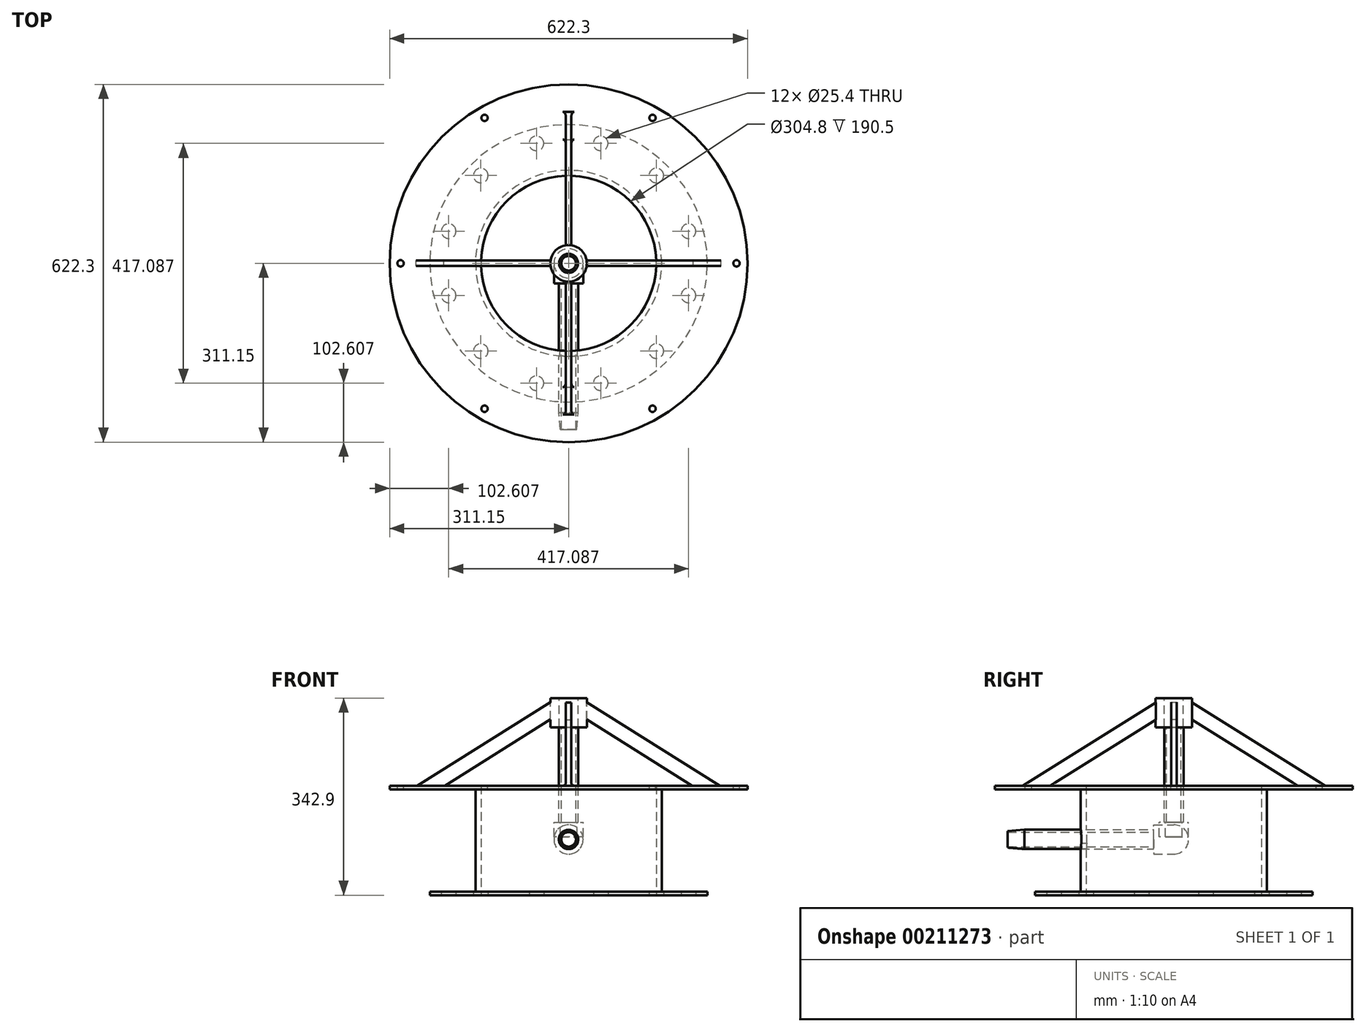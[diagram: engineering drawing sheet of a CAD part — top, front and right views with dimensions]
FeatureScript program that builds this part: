
annotation { "Feature Type Name" : "Feature", "Feature Type Description" : "" }
export const myFeature = defineFeature(function(context is Context, id is Id, definition is map)
    precondition{}
    {
        {
            var Q0;
            Q0=qCreatedBy(makeId("Top.planeOp"),FACE);
            var sketch = newSketch(context, id + "F0", { "sketchPlane" : qUnion([Q0])});
            skCircle(sketch, "E0", {"center": v(0, 0) * mm, "radius": 241.3 * mm});
            skCircle(sketch, "E1", {"center": v(0, 0) * mm, "radius": 152.4 * mm});
            skCircle(sketch, "E2", {"center": v(55.88, 208.54) * mm, "radius": 12.7 * mm});
            skCircle(sketch, "E3.1.0", {"center": v(-55.88, 208.54) * mm, "radius": 12.7 * mm});
            skCircle(sketch, "E3.2.0", {"center": v(-152.66, 152.66) * mm, "radius": 12.7 * mm});
            skCircle(sketch, "E3.3.0", {"center": v(-208.54, 55.88) * mm, "radius": 12.7 * mm});
            skCircle(sketch, "E3.4.0", {"center": v(-208.54, -55.88) * mm, "radius": 12.7 * mm});
            skCircle(sketch, "E3.5.0", {"center": v(-152.66, -152.66) * mm, "radius": 12.7 * mm});
            skCircle(sketch, "E3.6.0", {"center": v(-55.88, -208.54) * mm, "radius": 12.7 * mm});
            skCircle(sketch, "E3.7.0", {"center": v(55.88, -208.54) * mm, "radius": 12.7 * mm});
            skCircle(sketch, "E3.8.0", {"center": v(152.66, -152.66) * mm, "radius": 12.7 * mm});
            skCircle(sketch, "E3.9.0", {"center": v(208.54, -55.88) * mm, "radius": 12.7 * mm});
            skCircle(sketch, "E3.10.0", {"center": v(208.54, 55.88) * mm, "radius": 12.7 * mm});
            skCircle(sketch, "E3.11.0", {"center": v(152.66, 152.66) * mm, "radius": 12.7 * mm});
            skSolve(sketch);
        }
        {
            var Q0;
            Q0 = qSketchRegion(id + "F0", true);
            extrude(context, id + "F1", {"entities" : qUnion([Q0]), "depth" : 6.35 * mm});
        }
        {
            var Q0;
            Q0=makeQuery(id+"F1.opExtrude","CAP_FACE",FACE,{"disambiguationData":[OSD([sQuery(id+"F0.wireOp",EDGE,"E0"),sQuery(id+"F0.wireOp",EDGE,"E1"),sQuery(id+"F0.wireOp",EDGE,"E2"),sQuery(id+"F0.wireOp",EDGE,"E3.1.0"),sQuery(id+"F0.wireOp",EDGE,"E3.2.0"),sQuery(id+"F0.wireOp",EDGE,"E3.3.0"),sQuery(id+"F0.wireOp",EDGE,"E3.4.0"),sQuery(id+"F0.wireOp",EDGE,"E3.5.0"),sQuery(id+"F0.wireOp",EDGE,"E3.6.0"),sQuery(id+"F0.wireOp",EDGE,"E3.7.0"),sQuery(id+"F0.wireOp",EDGE,"E3.8.0"),sQuery(id+"F0.wireOp",EDGE,"E3.9.0"),sQuery(id+"F0.wireOp",EDGE,"E3.10.0"),sQuery(id+"F0.wireOp",EDGE,"E3.11.0")])],"isStart":false});
            var sketch = newSketch(context, id + "F2", { "sketchPlane" : qUnion([Q0])});
            skCircle(sketch, "E4", {"center": v(0, 0) * mm, "radius": 152.4 * mm});
            skCircle(sketch, "E5", {"center": v(0, 0) * mm, "radius": 161.93 * mm});
            skSolve(sketch);
        }
        {
            var Q0;
            Q0 = qSketchRegion(id + "F2", true);
            extrude(context, id + "F3", {"entities" : qUnion([Q0]), "operationType" : NewBodyOperationType.ADD, "depth" : 177.8 * mm});
        }
        {
            var Q0;
            Q0=makeQuery(id+"F3.opExtrude","CAP_FACE",FACE,{"disambiguationData":[OSD([sQuery(id+"F2.wireOp",EDGE,"E4"),sQuery(id+"F2.wireOp",EDGE,"E5")])],"isStart":false});
            var sketch = newSketch(context, id + "F4", { "sketchPlane" : qUnion([Q0])});
            skCircle(sketch, "E6", {"center": v(0, 0) * mm, "radius": 311.15 * mm});
            skCircle(sketch, "E7", {"center": v(0, 0) * mm, "radius": 152.4 * mm});
            skSolve(sketch);
        }
        {
            var Q0;
            Q0 = qSketchRegion(id + "F4", true);
            extrude(context, id + "F5", {"entities" : qUnion([Q0]), "operationType" : NewBodyOperationType.ADD, "depth" : 6.35 * mm});
        }
        {
            var Q0;
            Q0=makeQuery(id+"F5.opExtrude","CAP_FACE",FACE,{"disambiguationData":[OSD([sQuery(id+"F4.wireOp",EDGE,"E6"),sQuery(id+"F4.wireOp",EDGE,"E7")])],"isStart":false});
            var sketch = newSketch(context, id + "F6", { "sketchPlane" : qUnion([Q0])});
            skCircle(sketch, "E8", {"center": v(146.05, 252.97) * mm, "radius": 5.56 * mm});
            skCircle(sketch, "E9.1.0", {"center": v(-146.05, 252.97) * mm, "radius": 5.56 * mm});
            skCircle(sketch, "E9.2.0", {"center": v(-292.1, 0) * mm, "radius": 5.56 * mm});
            skCircle(sketch, "E9.3.0", {"center": v(-146.05, -252.97) * mm, "radius": 5.56 * mm});
            skCircle(sketch, "E9.4.0", {"center": v(146.05, -252.97) * mm, "radius": 5.56 * mm});
            skCircle(sketch, "E9.5.0", {"center": v(292.1, 0) * mm, "radius": 5.56 * mm});
            skPoint(sketch, "E9.center", {"position": v(0, 0) * mm});
            skSolve(sketch);
        }
        {
            var Q0;
            Q0 = qSketchRegion(id + "F6", true);
            extrude(context, id + "F7", {"entities" : qUnion([Q0]), "operationType" : NewBodyOperationType.REMOVE, "oppositeDirection" : true, "depth" : 25.4 * mm});
        }
        {
            var Q0;
            Q0=makeQuery(id+"F5.opExtrude","CAP_FACE",FACE,{"disambiguationData":[OSD([sQuery(id+"F4.wireOp",EDGE,"E6"),sQuery(id+"F4.wireOp",EDGE,"E7")])],"isStart":false});
            cPlane(context, id + "F8", {"entities" : qUnion([Q0]), "cplaneType" : CPlaneType.OFFSET, "offset" : 152.4 * mm, "width" : 152.4 * mm, "height" : 152.4 * mm});
        }
        {
            var Q0;
            Q0=qCreatedBy(id+"F8.planeOp",FACE);
            var sketch = newSketch(context, id + "F9", { "sketchPlane" : qUnion([Q0])});
            skCircle(sketch, "E10", {"center": v(0, 0) * mm, "radius": 16.51 * mm});
            skCircle(sketch, "E11", {"center": v(0, 0) * mm, "radius": 31.75 * mm});
            skSolve(sketch);
        }
        {
            var Q0;
            Q0 = qSketchRegion(id + "F9", true);
            extrude(context, id + "F10", {"entities" : qUnion([Q0]), "oppositeDirection" : true, "depth" : 50.8 * mm});
        }
        {
            var Q0;
            Q0=qCreatedBy(makeId("Front.planeOp"),FACE);
            var sketch = newSketch(context, id + "F11", { "sketchPlane" : qUnion([Q0])});
            skLineSegment(sketch, "E12", {"start": v(-31.31, 335.52) * mm, "end": v(-264.9, 189.3) * mm});
            skLineSegment(sketch, "E13", {"start": v(-264.9, 189.3) * mm, "end": v(-217.03, 189.3) * mm});
            skLineSegment(sketch, "E14", {"start": v(-217.03, 189.3) * mm, "end": v(-31.31, 305.55) * mm});
            skLineSegment(sketch, "E15", {"start": v(-31.31, 305.55) * mm, "end": v(-31.31, 335.52) * mm});
            skLineSegment(sketch, "E16", {"start": v(0, 0) * mm, "end": v(0, 440.85) * mm});
            skLineSegment(sketch, "E17.MirrorCS", {"start": v(217.03, 189.3) * mm, "end": v(31.31, 305.55) * mm});
            skLineSegment(sketch, "E18.MirrorCS", {"start": v(31.31, 335.52) * mm, "end": v(264.9, 189.3) * mm});
            skLineSegment(sketch, "E19.MirrorCS", {"start": v(31.31, 305.55) * mm, "end": v(31.31, 335.52) * mm});
            skLineSegment(sketch, "E20.MirrorCS", {"start": v(264.9, 189.3) * mm, "end": v(217.03, 189.3) * mm});
            skSolve(sketch);
        }
        {
            var Q0;
            Q0=makeQuery(id+"F11.imprint","IMPRINT",FACE,{"disambiguationData":[TD([[makeQuery(id+"F11.imprint","IMPRINT",EDGE,{"derivedFrom":sQuery(id+"F11.wireOp",EDGE,"E12")}),1.0]])]});
            var Q1;
            Q1=makeQuery(id+"F11.imprint","IMPRINT",FACE,{"disambiguationData":[TD([[makeQuery(id+"F11.imprint","IMPRINT",EDGE,{"derivedFrom":sQuery(id+"F11.wireOp",EDGE,"E17.MirrorCS")}),-1.0]])]});
            extrude(context, id + "F12", {"entities" : qUnion([Q0, Q1]), "endBound" : BoundingType.SYMMETRIC, "depth" : 9.52 * mm});
        }
        {
            var Q0;
            Q0=makeQuery(id+"F12.opExtrude","SWEPT_BODY",BODY,{"disambiguationData":[OSD([sQuery(id+"F11.wireOp",EDGE,"E12"),sQuery(id+"F11.wireOp",EDGE,"E13"),sQuery(id+"F11.wireOp",EDGE,"E14"),sQuery(id+"F11.wireOp",EDGE,"E15")])]});
            transform(context, id + "F13", {"entities" : qUnion([Q0]), "transformType" : TransformType.TRANSLATION_3D, "dx" : 0 * mm, "dy" : 0 * mm, "dz" : 0 * mm, "makeCopy" : true});
        }
        {
            var Q0;
            Q0=qCreatedBy(makeId("Right.planeOp"),FACE);
            var sketch = newSketch(context, id + "F14", { "sketchPlane" : qUnion([Q0])});
            skLineSegment(sketch, "E21", {"start": v(31.26, 335.41) * mm, "end": v(263.35, 190.48) * mm});
            skLineSegment(sketch, "E22", {"start": v(263.35, 190.48) * mm, "end": v(215.4, 190.48) * mm});
            skLineSegment(sketch, "E23", {"start": v(215.4, 190.48) * mm, "end": v(31.26, 305.47) * mm});
            skLineSegment(sketch, "E24", {"start": v(31.26, 305.47) * mm, "end": v(31.26, 335.41) * mm});
            skLineSegment(sketch, "E25", {"start": v(0, 360.57) * mm, "end": v(0, 151.37) * mm});
            skLineSegment(sketch, "E26.MirrorCS", {"start": v(-215.4, 190.48) * mm, "end": v(-31.26, 305.47) * mm});
            skLineSegment(sketch, "E27.MirrorCS", {"start": v(-31.26, 335.41) * mm, "end": v(-263.35, 190.48) * mm});
            skLineSegment(sketch, "E28.MirrorCS", {"start": v(-31.26, 305.47) * mm, "end": v(-31.26, 335.41) * mm});
            skLineSegment(sketch, "E29.MirrorCS", {"start": v(-263.35, 190.48) * mm, "end": v(-215.4, 190.48) * mm});
            skSolve(sketch);
        }
        {
            var Q0;
            Q0 = qSketchRegion(id + "F14", true);
            extrude(context, id + "F15", {"entities" : qUnion([Q0]), "operationType" : NewBodyOperationType.ADD, "endBound" : BoundingType.SYMMETRIC, "depth" : 9.52 * mm});
        }
        {
            var Q0;
            Q0=makeQuery(id+"F15.boolean.opBoolean","INTERSECT",EDGE,{"derivedFrom":[makeQuery(id+"F5.opExtrude","CAP_FACE",FACE,{"disambiguationData":[OSD([sQuery(id+"F4.wireOp",EDGE,"E6"),sQuery(id+"F4.wireOp",EDGE,"E7")])],"isStart":false}),makeQuery(id+"F15.opExtrude","CAP_FACE",FACE,{"disambiguationData":[OSD([sQuery(id+"F14.wireOp",EDGE,"E21"),sQuery(id+"F14.wireOp",EDGE,"E22"),sQuery(id+"F14.wireOp",EDGE,"E23"),sQuery(id+"F14.wireOp",EDGE,"E24")])],"isStart":true})]});
            var Q1;
            Q1=makeQuery(id+"F15.boolean.opBoolean","INTERSECT",EDGE,{"derivedFrom":[makeQuery(id+"F5.opExtrude","CAP_FACE",FACE,{"disambiguationData":[OSD([sQuery(id+"F4.wireOp",EDGE,"E6"),sQuery(id+"F4.wireOp",EDGE,"E7")])],"isStart":false}),makeQuery(id+"F15.opExtrude","CAP_FACE",FACE,{"disambiguationData":[OSD([sQuery(id+"F14.wireOp",EDGE,"E21"),sQuery(id+"F14.wireOp",EDGE,"E22"),sQuery(id+"F14.wireOp",EDGE,"E23"),sQuery(id+"F14.wireOp",EDGE,"E24")])],"isStart":false})]});
            var Q2;
            Q2=makeQuery(id+"F15.boolean.opBoolean","INTERSECT",EDGE,{"derivedFrom":[makeQuery(id+"F5.opExtrude","CAP_FACE",FACE,{"disambiguationData":[OSD([sQuery(id+"F4.wireOp",EDGE,"E6"),sQuery(id+"F4.wireOp",EDGE,"E7")])],"isStart":false}),makeQuery(id+"F15.opExtrude","CAP_FACE",FACE,{"disambiguationData":[OSD([sQuery(id+"F14.wireOp",EDGE,"E26.MirrorCS"),sQuery(id+"F14.wireOp",EDGE,"E27.MirrorCS"),sQuery(id+"F14.wireOp",EDGE,"E28.MirrorCS"),sQuery(id+"F14.wireOp",EDGE,"E29.MirrorCS")])],"isStart":true})]});
            var Q3;
            Q3=makeQuery(id+"F15.boolean.opBoolean","INTERSECT",EDGE,{"derivedFrom":[makeQuery(id+"F5.opExtrude","CAP_FACE",FACE,{"disambiguationData":[OSD([sQuery(id+"F4.wireOp",EDGE,"E6"),sQuery(id+"F4.wireOp",EDGE,"E7")])],"isStart":false}),makeQuery(id+"F15.opExtrude","CAP_FACE",FACE,{"disambiguationData":[OSD([sQuery(id+"F14.wireOp",EDGE,"E26.MirrorCS"),sQuery(id+"F14.wireOp",EDGE,"E27.MirrorCS"),sQuery(id+"F14.wireOp",EDGE,"E28.MirrorCS"),sQuery(id+"F14.wireOp",EDGE,"E29.MirrorCS")])],"isStart":false})]});
            fillet(context, id + "F16", {"entities" : qUnion([Q0, Q1, Q2, Q3]), "radius" : 5.08 * mm, "tangentPropagation" : true, "allowEdgeOverflow" : false});
        }
        {
            var Q0;
            Q0=qCreatedBy(makeId("Front.planeOp"),FACE);
            cPlane(context, id + "F17", {"entities" : qUnion([Q0]), "cplaneType" : CPlaneType.OFFSET, "offset" : 161.92 * mm, "width" : 152.4 * mm, "height" : 152.4 * mm});
        }
        {
            var Q0;
            Q0=qCreatedBy(id+"F17.planeOp",FACE);
            var sketch = newSketch(context, id + "F18", { "sketchPlane" : qUnion([Q0])});
            skCircle(sketch, "E30", {"center": v(0, 96.94) * mm, "radius": 16.7 * mm});
            skSolve(sketch);
        }
        {
            var Q0;
            Q0 = qSketchRegion(id + "F18", true);
            extrude(context, id + "F19", {"entities" : qUnion([Q0]), "operationType" : NewBodyOperationType.REMOVE, "oppositeDirection" : true, "depth" : 25.4 * mm});
        }
        {
            var Q0;
            Q0=qCreatedBy(id+"F17.planeOp",FACE);
            var sketch = newSketch(context, id + "F20", { "sketchPlane" : qUnion([Q0])});
            skCircle(sketch, "E31", {"center": v(0, 97.03) * mm, "radius": 16.74 * mm});
            skCircle(sketch, "E32", {"center": v(0, 97.03) * mm, "radius": 12.7 * mm});
            skSolve(sketch);
        }
        {
            var Q0;
            Q0 = qSketchRegion(id + "F20", true);
            extrude(context, id + "F21", {"entities" : qUnion([Q0]), "operationType" : NewBodyOperationType.ADD, "endBound" : BoundingType.SYMMETRIC, "depth" : 254 * mm});
        }
        {
            var Q0;
            Q0=makeQuery(id+"F21.opExtrude","CAP_EDGE",EDGE,{"disambiguationData":[OSD([sQuery(id+"F20.wireOp",EDGE,"E31")])],"isStart":false});
            chamfer(context, id + "F22", {"entities" : qUnion([Q0]), "chamferType" : ChamferType.OFFSET_ANGLE, "width" : 2.54 * mm, "oppositeDirection" : false, "angle" : 85 * degree, "tangentPropagation" : true});
        }
        {
            var Q0;
            Q0=makeQuery(id+"F10.opExtrude","CAP_FACE",FACE,{"disambiguationData":[OSD([sQuery(id+"F9.wireOp",EDGE,"E10"),sQuery(id+"F9.wireOp",EDGE,"E11")])],"isStart":false});
            var sketch = newSketch(context, id + "F23", { "sketchPlane" : qUnion([Q0])});
            skCircle(sketch, "E33", {"center": v(0, 0) * mm, "radius": 16.74 * mm});
            skCircle(sketch, "E34", {"center": v(0, 0) * mm, "radius": 12.7 * mm});
            skSolve(sketch);
        }
        {
            var Q0;
            Q0 = qSketchRegion(id + "F23", true);
            extrude(context, id + "F24", {"entities" : qUnion([Q0]), "operationType" : NewBodyOperationType.ADD, "depth" : 165.1 * mm});
        }
        {
            var Q0;
            Q0=makeQuery(id+"F24.opExtrude","CAP_FACE",FACE,{"disambiguationData":[OSD([sQuery(id+"F23.wireOp",EDGE,"E33"),sQuery(id+"F23.wireOp",EDGE,"E34")])],"isStart":false});
            var sketch = newSketch(context, id + "F25", { "sketchPlane" : qUnion([Q0])});
            skCircle(sketch, "E35", {"center": v(0, 0) * mm, "radius": 14.6 * mm});
            skLineSegment(sketch, "E36.bottom", {"start": v(-25.4, 25.4) * mm, "end": v(25.4, 25.4) * mm});
            skLineSegment(sketch, "E36.top", {"start": v(-25.4, -25.4) * mm, "end": v(25.4, -25.4) * mm});
            skLineSegment(sketch, "E36.left", {"start": v(-25.4, 25.4) * mm, "end": v(-25.4, -25.4) * mm});
            skLineSegment(sketch, "E36.right", {"start": v(25.4, 25.4) * mm, "end": v(25.4, -25.4) * mm});
            skSolve(sketch);
        }
        {
            var Q0;
            Q0 = qSketchRegion(id + "F25", true);
            extrude(context, id + "F26", {"entities" : qUnion([Q0]), "operationType" : NewBodyOperationType.ADD, "depth" : 25.4 * mm});
        }
        {
            var Q0;
            Q0=makeQuery(id+"F21.opExtrude","CAP_FACE",FACE,{"disambiguationData":[OSD([sQuery(id+"F20.wireOp",EDGE,"E31"),sQuery(id+"F20.wireOp",EDGE,"E32")])],"isStart":true});
            var sketch = newSketch(context, id + "F27", { "sketchPlane" : qUnion([Q0])});
            skLineSegment(sketch, "E37.bottom", {"start": v(25.4, 122.43) * mm, "end": v(-25.4, 122.43) * mm});
            skLineSegment(sketch, "E37.top", {"start": v(25.4, 71.63) * mm, "end": v(-25.4, 71.63) * mm});
            skLineSegment(sketch, "E37.left", {"start": v(25.4, 122.43) * mm, "end": v(25.4, 71.63) * mm});
            skLineSegment(sketch, "E37.right", {"start": v(-25.4, 122.43) * mm, "end": v(-25.4, 71.63) * mm});
            skPoint(sketch, "E37.middle", {"position": v(0, 97.03) * mm});
            skSolve(sketch);
        }
        {
            var Q0;
            Q0 = qSketchRegion(id + "F27", true);
            extrude(context, id + "F28", {"entities" : qUnion([Q0]), "depth" : 60.32 * mm});
        }
        {
            var Q0;
            Q0=makeQuery(id+"F28.opExtrude","CAP_EDGE",EDGE,{"disambiguationData":[OSD([sQuery(id+"F27.wireOp",EDGE,"E37.top")])],"isStart":false});
            var Q1;
            Q1=makeQuery(id+"F28.opExtrude","SWEPT_EDGE",EDGE,{"disambiguationData":[OSD([sQuery(id+"F27.wireOp",EDGE,"E37.top"),sQuery(id+"F27.wireOp",EDGE,"E37.right")])]});
            var Q2;
            Q2=makeQuery(id+"F28.opExtrude","SWEPT_EDGE",EDGE,{"disambiguationData":[OSD([sQuery(id+"F27.wireOp",EDGE,"E37.top"),sQuery(id+"F27.wireOp",EDGE,"E37.left")])]});
            var Q3;
            Q3=makeQuery(id+"F26.opExtrude","SWEPT_EDGE",EDGE,{"disambiguationData":[OSD([sQuery(id+"F25.wireOp",EDGE,"E36.top"),sQuery(id+"F25.wireOp",EDGE,"E36.left")])]});
            var Q4;
            Q4=makeQuery(id+"F26.opExtrude","SWEPT_EDGE",EDGE,{"disambiguationData":[OSD([sQuery(id+"F25.wireOp",EDGE,"E36.top"),sQuery(id+"F25.wireOp",EDGE,"E36.right")])]});
            fillet(context, id + "F29", {"entities" : qUnion([Q0, Q1, Q2, Q3, Q4]), "radius" : 25.4 * mm, "tangentPropagation" : true, "allowEdgeOverflow" : false});
        }
        {
            var Q0;
            Q0=makeQuery(id+"F28.opExtrude","CAP_EDGE",EDGE,{"disambiguationData":[OSD([sQuery(id+"F27.wireOp",EDGE,"E37.right")])],"isStart":false});
            var Q1;
            Q1=makeQuery(id+"F28.opExtrude","CAP_EDGE",EDGE,{"disambiguationData":[OSD([sQuery(id+"F27.wireOp",EDGE,"E37.left")])],"isStart":false});
            fillet(context, id + "F30", {"entities" : qUnion([Q0, Q1]), "radius" : 25.4 * mm, "tangentPropagation" : true, "allowEdgeOverflow" : false});
        }
        {
            var Q0;
            Q0=makeQuery(id+"F28.opExtrude","SWEPT_EDGE",EDGE,{"disambiguationData":[OSD([sQuery(id+"F27.wireOp",EDGE,"E37.bottom"),sQuery(id+"F27.wireOp",EDGE,"E37.right")])]});
            var Q1;
            Q1=makeQuery(id+"F26.opExtrude","SWEPT_EDGE",EDGE,{"disambiguationData":[OSD([sQuery(id+"F25.wireOp",EDGE,"E36.bottom"),sQuery(id+"F25.wireOp",EDGE,"E36.right")])]});
            var Q2;
            Q2=makeQuery(id+"F26.opExtrude","SWEPT_EDGE",EDGE,{"disambiguationData":[OSD([sQuery(id+"F25.wireOp",EDGE,"E36.bottom"),sQuery(id+"F25.wireOp",EDGE,"E36.left")])]});
            fillet(context, id + "F31", {"entities" : qUnion([Q0, Q1, Q2]), "radius" : 25.4 * mm, "tangentPropagation" : true, "allowEdgeOverflow" : false});
        }
    });
